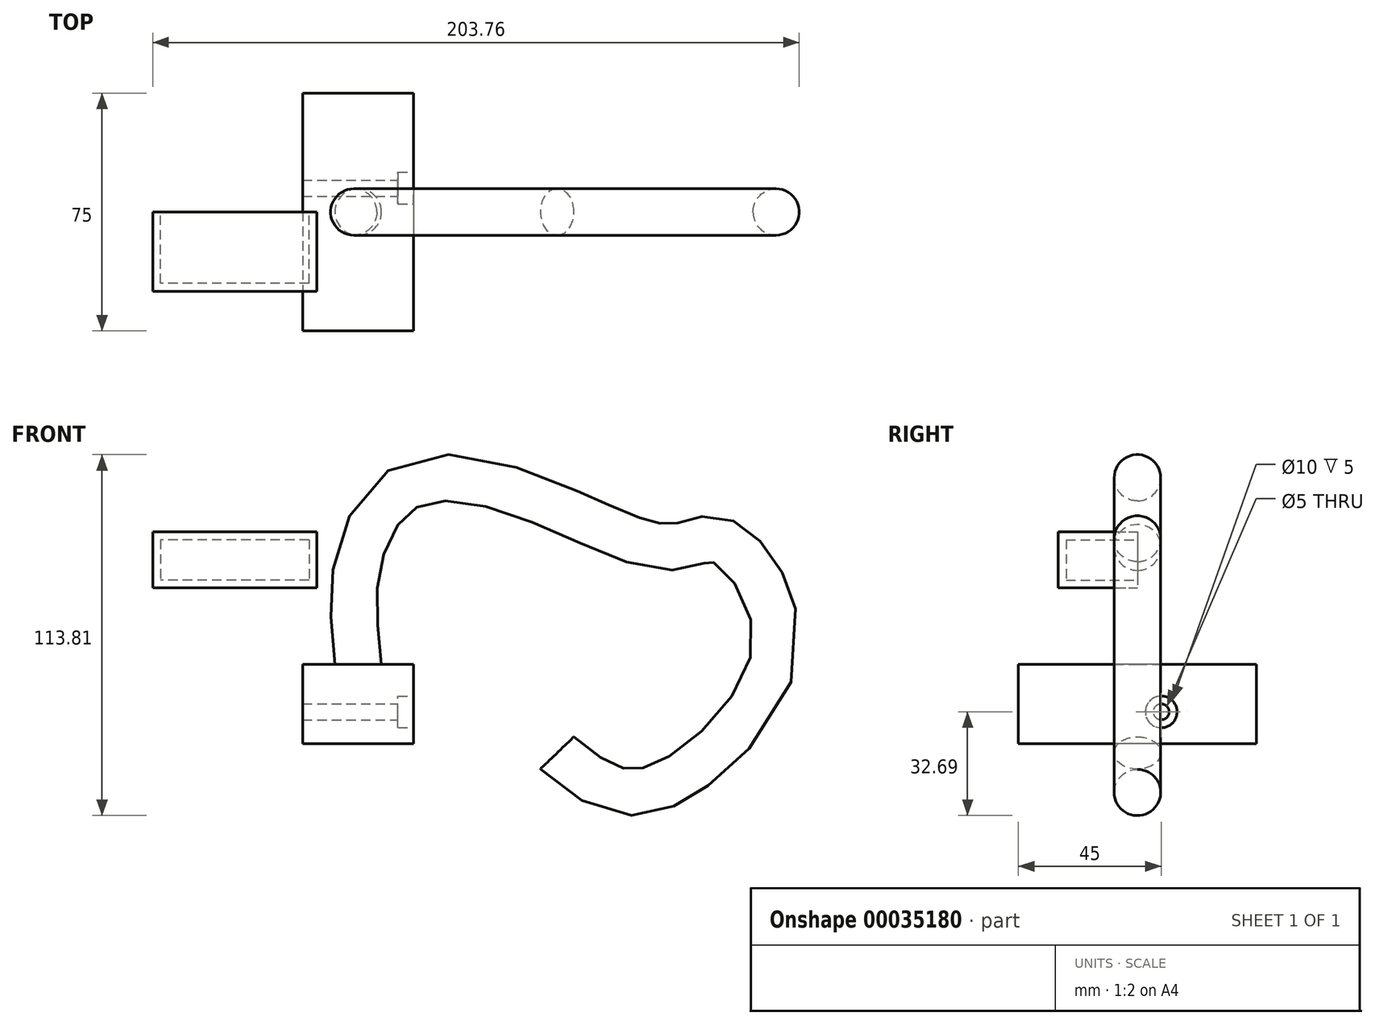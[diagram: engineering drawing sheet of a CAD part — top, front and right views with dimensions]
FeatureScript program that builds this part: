
annotation { "Feature Type Name" : "Feature", "Feature Type Description" : "" }
export const myFeature = defineFeature(function(context is Context, id is Id, definition is map)
    precondition{}
    {
        {
            var Q0;
            Q0=qCreatedBy(makeId("Top.planeOp"),FACE);
            var sketch = newSketch(context, id + "F0", { "sketchPlane" : qUnion([Q0])});
            skLineSegment(sketch, "E0.bottom", {"start": v(-17.5, 37.5) * mm, "end": v(17.5, 37.5) * mm});
            skLineSegment(sketch, "E0.top", {"start": v(-17.5, -37.5) * mm, "end": v(17.5, -37.5) * mm});
            skLineSegment(sketch, "E0.left", {"start": v(-17.5, 37.5) * mm, "end": v(-17.5, -37.5) * mm});
            skLineSegment(sketch, "E0.right", {"start": v(17.5, 37.5) * mm, "end": v(17.5, -37.5) * mm});
            skLineSegment(sketch, "E1", {"start": v(-17.5, 37.5) * mm, "end": v(17.5, -37.5) * mm, "construction": true});
            skSolve(sketch);
        }
        {
            var Q0;
            Q0=makeQuery(id+"F0.imprint","IMPRINT",FACE,{"disambiguationData":[TD([[makeQuery(id+"F0.imprint","IMPRINT",EDGE,{"derivedFrom":sQuery(id+"F0.wireOp",EDGE,"E0.bottom")}),-1.0]])]});
            extrude(context, id + "F1", {"entities" : qUnion([Q0]), "oppositeDirection" : true, "depth" : 25 * mm});
        }
        {
            var Q0;
            Q0=makeQuery(id+"F1.opExtrude","SWEPT_FACE",FACE,{"disambiguationData":[OSD([sQuery(id+"F0.wireOp",EDGE,"E0.right")])]});
            var sketch = newSketch(context, id + "F2", { "sketchPlane" : qUnion([Q0])});
            skCircle(sketch, "E2", {"center": v(7.5, -15) * mm, "radius": 5 * mm});
            skCircle(sketch, "E3", {"center": v(7.5, -15) * mm, "radius": 2.5 * mm});
            skSolve(sketch);
        }
        {
            var Q0;
            Q0=makeQuery(id+"F2.imprint","IMPRINT",FACE,{"disambiguationData":[TD([[makeQuery(id+"F2.imprint","IMPRINT",EDGE,{"derivedFrom":sQuery(id+"F2.wireOp",EDGE,"E2")}),1.0]])]});
            extrude(context, id + "F3", {"entities" : qUnion([Q0]), "operationType" : NewBodyOperationType.REMOVE, "oppositeDirection" : true, "depth" : 5 * mm});
        }
        {
            var Q0;
            Q0=makeQuery(id+"F3.boolean.opBoolean","SPLIT",FACE,{"disambiguationData":[TD([makeQuery(id+"F3.opExtrude","SWEPT_FACE",FACE,{"disambiguationData":[OSD([sQuery(id+"F2.wireOp",EDGE,"E3")])]})])],"derivedFrom":makeQuery(id+"F1.opExtrude","SWEPT_FACE",FACE,{"disambiguationData":[OSD([sQuery(id+"F0.wireOp",EDGE,"E0.right")])]})});
            extrude(context, id + "F4", {"entities" : qUnion([Q0]), "operationType" : NewBodyOperationType.REMOVE, "endBound" : BoundingType.THROUGH_ALL, "oppositeDirection" : true, "depth" : 25 * mm});
        }
        {
            var Q0;
            Q0=qCreatedBy(makeId("Front.planeOp"),FACE);
            var sketch = newSketch(context, id + "F5", { "sketchPlane" : qUnion([Q0])});
            skFitSpline(sketch, "E4", {"points": [v(0, 0) * mm, v(0, 32.8) * mm, v(16.51, 56.68) * mm, v(57.52, 51.63) * mm, v(98.68, 36.94) * mm, v(113.98, 39.08) * mm, v(131.72, 8.18) * mm, v(106.02, -32.37) * mm, v(82.46, -40.02) * mm, v(62.72, -27.93) * mm], "startDerivative": vector(-31.9, 293.5) * mm, "endDerivative": vector(-202.55, 169.3) * mm});
            skSolve(sketch);
        }
        {
            var Q0;
            Q0=makeQuery(id+"F1.opExtrude","CAP_FACE",FACE,{"disambiguationData":[OSD([sQuery(id+"F0.wireOp",EDGE,"E0.bottom"),sQuery(id+"F0.wireOp",EDGE,"E0.top"),sQuery(id+"F0.wireOp",EDGE,"E0.left"),sQuery(id+"F0.wireOp",EDGE,"E0.right")])],"isStart":true});
            var sketch = newSketch(context, id + "F6", { "sketchPlane" : qUnion([Q0])});
            skCircle(sketch, "E5", {"center": v(0, 0) * mm, "radius": 7.33 * mm});
            skSolve(sketch);
        }
        {
            var Q0;
            Q0=makeQuery(id+"F6.imprint","IMPRINT",FACE,{"disambiguationData":[TD([[makeQuery(id+"F6.imprint","IMPRINT",EDGE,{"derivedFrom":sQuery(id+"F6.wireOp",EDGE,"E5")}),1.0]])]});
            var Q1;
            Q1=sQuery(id+"F5.wireOp",EDGE,"E4");
            sweep(context, id + "F7", {"operationType" : NewBodyOperationType.ADD, "profiles" : qUnion([Q0]), "path" : qUnion([Q1])});
        }
        {
            var Q0;
            Q0=qCreatedBy(makeId("Front.planeOp"),FACE);
            var sketch = newSketch(context, id + "F8", { "sketchPlane" : qUnion([Q0])});
            skLineSegment(sketch, "E6.bottom", {"start": v(-12.97, 41.8) * mm, "end": v(-64.74, 41.8) * mm});
            skLineSegment(sketch, "E6.top", {"start": v(-12.97, 24.07) * mm, "end": v(-64.74, 24.07) * mm});
            skLineSegment(sketch, "E6.left", {"start": v(-12.97, 41.8) * mm, "end": v(-12.97, 24.07) * mm});
            skLineSegment(sketch, "E6.right", {"start": v(-64.74, 41.8) * mm, "end": v(-64.74, 24.07) * mm});
            skSolve(sketch);
        }
        {
            var Q0;
            Q0=makeQuery(id+"F8.imprint","IMPRINT",FACE,{"disambiguationData":[TD([[makeQuery(id+"F8.imprint","IMPRINT",EDGE,{"derivedFrom":sQuery(id+"F8.wireOp",EDGE,"E6.bottom")}),1.0]])]});
            extrude(context, id + "F9", {"entities" : qUnion([Q0]), "depth" : 25 * mm});
        }
        {
            var Q0;
            Q0=makeQuery(id+"F9.opExtrude","CAP_FACE",FACE,{"disambiguationData":[OSD([sQuery(id+"F8.wireOp",EDGE,"E6.bottom"),sQuery(id+"F8.wireOp",EDGE,"E6.top"),sQuery(id+"F8.wireOp",EDGE,"E6.left"),sQuery(id+"F8.wireOp",EDGE,"E6.right")])],"isStart":true});
            shell(context, id + "F10", {"entities" : qUnion([Q0]), "thickness" : 2.5 * mm});
        }
    });
